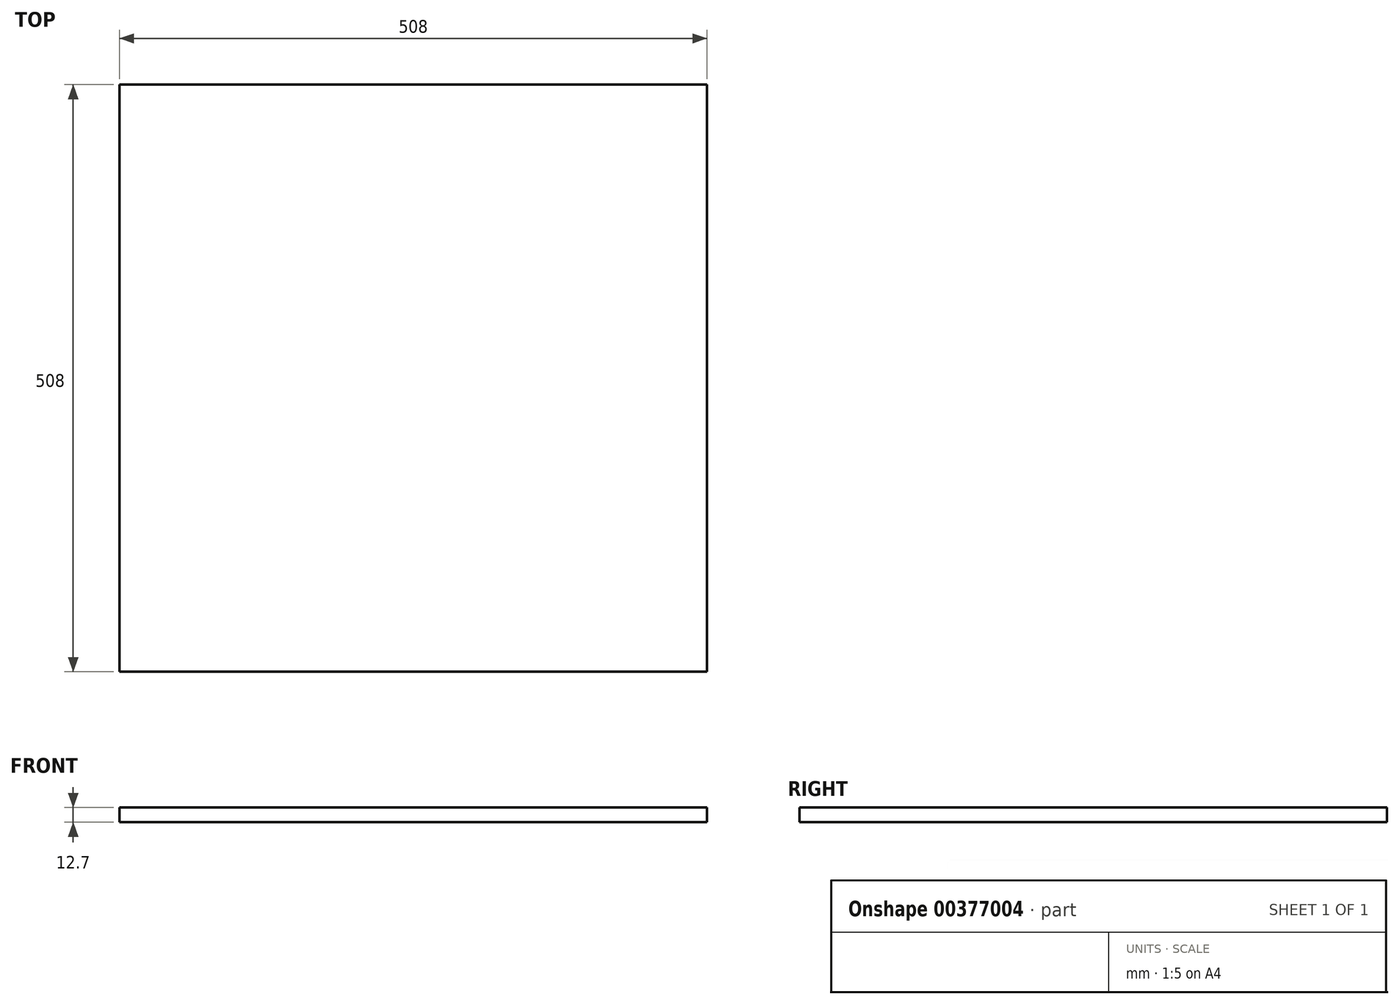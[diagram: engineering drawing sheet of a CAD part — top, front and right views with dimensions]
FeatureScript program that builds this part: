
annotation { "Feature Type Name" : "Feature", "Feature Type Description" : "" }
export const myFeature = defineFeature(function(context is Context, id is Id, definition is map)
    precondition{}
    {
        {
            var Q0;
            Q0=qCreatedBy(makeId("Top.planeOp"),FACE);
            var sketch = newSketch(context, id + "F0", { "sketchPlane" : qUnion([Q0])});
            skLineSegment(sketch, "E0.bottom", {"start": v(254, 254) * mm, "end": v(-254, 254) * mm});
            skLineSegment(sketch, "E0.top", {"start": v(254, -254) * mm, "end": v(-254, -254) * mm});
            skLineSegment(sketch, "E0.left", {"start": v(254, 254) * mm, "end": v(254, -254) * mm});
            skLineSegment(sketch, "E0.right", {"start": v(-254, 254) * mm, "end": v(-254, -254) * mm});
            skPoint(sketch, "E0.middle", {"position": v(0, 0) * mm});
            skSolve(sketch);
        }
        {
            var Q0;
            Q0=makeQuery(id+"F0.imprint","IMPRINT",FACE,{"disambiguationData":[TD([[makeQuery(id+"F0.imprint","IMPRINT",EDGE,{"derivedFrom":sQuery(id+"F0.wireOp",EDGE,"E0.bottom")}),1.0]])]});
            extrude(context, id + "F1", {"entities" : qUnion([Q0]), "depth" : 12.7 * mm});
        }
    });
